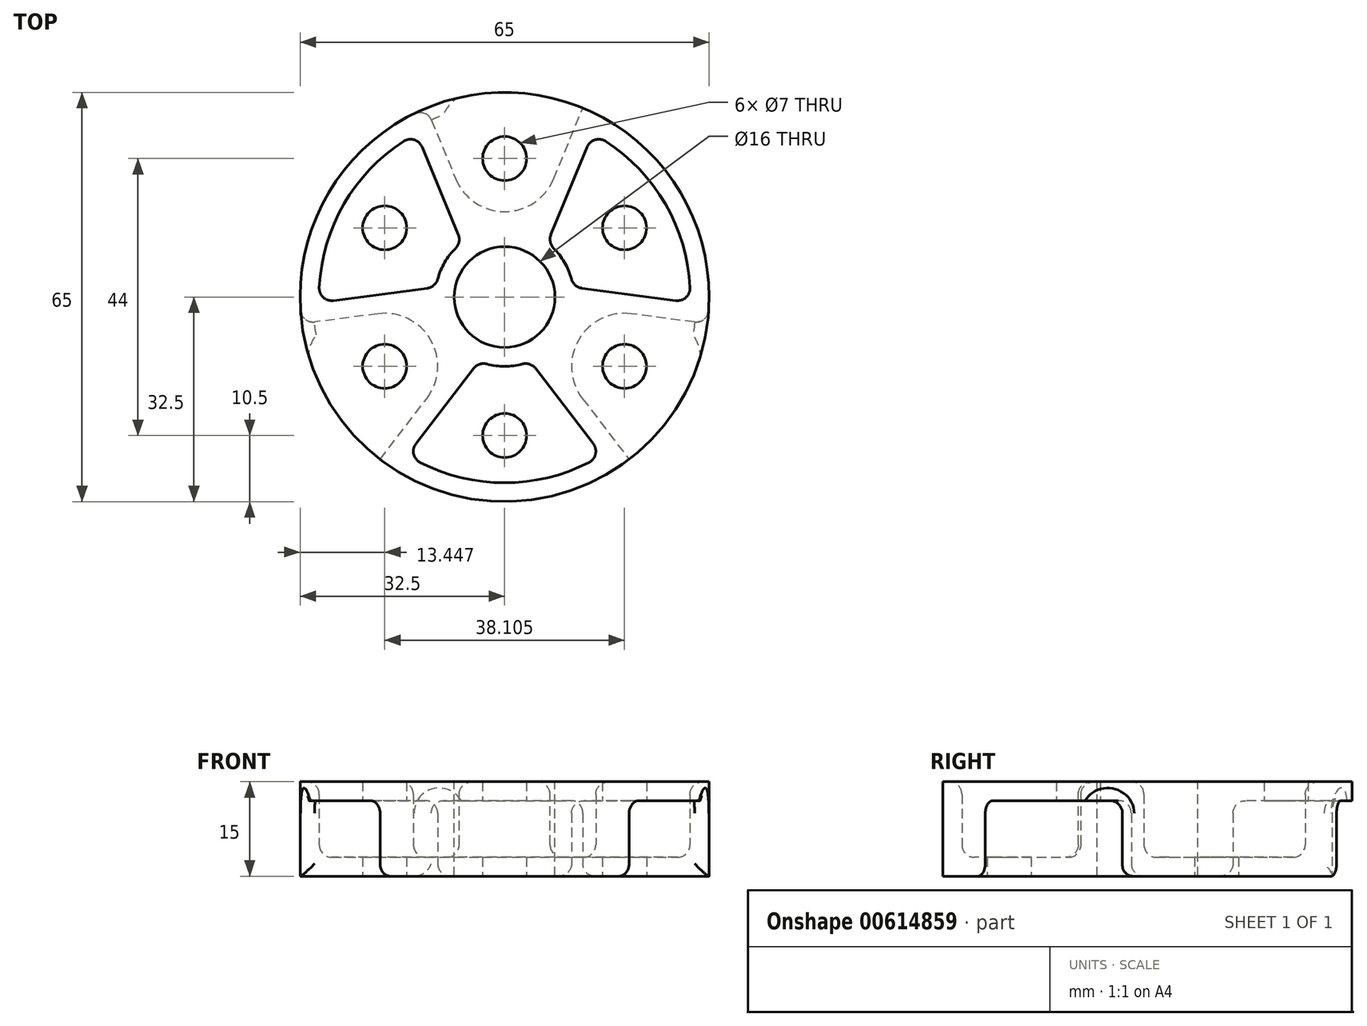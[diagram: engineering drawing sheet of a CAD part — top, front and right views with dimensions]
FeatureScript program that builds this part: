
annotation { "Feature Type Name" : "Feature", "Feature Type Description" : "" }
export const myFeature = defineFeature(function(context is Context, id is Id, definition is map)
    precondition{}
    {
        {
            var Q0;
            Q0=qCreatedBy(makeId("Top.planeOp"),FACE);
            var sketch = newSketch(context, id + "F0", { "sketchPlane" : qUnion([Q0])});
            skCircle(sketch, "E0", {"center": v(0, 0) * mm, "radius": 32.5 * mm});
            skCircle(sketch, "E1", {"center": v(0, 0) * mm, "radius": 8 * mm});
            skCircle(sketch, "E2", {"center": v(19.05, 11) * mm, "radius": 3.5 * mm});
            skCircle(sketch, "E3", {"center": v(0, 0) * mm, "radius": 22 * mm, "construction": true});
            skCircle(sketch, "E4.1.0", {"center": v(0, 22) * mm, "radius": 3.5 * mm});
            skCircle(sketch, "E4.2.0", {"center": v(-19.05, 11) * mm, "radius": 3.5 * mm});
            skCircle(sketch, "E4.3.0", {"center": v(-19.05, -11) * mm, "radius": 3.5 * mm});
            skLineSegment(sketch, "E5", {"start": v(-12.44, 30.03) * mm, "end": v(-7.78, 18.78) * mm});
            skArc(sketch, "E6", {"start": v(-7.78, 18.78) * mm, "mid": v(0, 13.58) * mm, "end": v(7.78, 18.78) * mm});
            skLineSegment(sketch, "E7", {"start": v(7.78, 18.78) * mm, "end": v(12.44, 30.03) * mm});
            skLineSegment(sketch, "E8.1.0", {"start": v(-20.15, -2.65) * mm, "end": v(-32.22, -4.24) * mm});
            skArc(sketch, "E8.1.1", {"start": v(-12.37, -16.13) * mm, "mid": v(-11.76, -6.8) * mm, "end": v(-20.15, -2.65) * mm});
            skLineSegment(sketch, "E8.1.2", {"start": v(-19.78, -25.78) * mm, "end": v(-12.37, -16.13) * mm});
            skCircle(sketch, "E9.0", {"center": v(0, 0) * mm, "radius": 29.5 * mm});
            skLineSegment(sketch, "E10.0", {"start": v(10.55, 17.63) * mm, "end": v(15.16, 28.75) * mm});
            skArc(sketch, "E10.1", {"start": v(-10.55, 17.63) * mm, "mid": v(0, 10.58) * mm, "end": v(10.55, 17.63) * mm});
            skLineSegment(sketch, "E10.2", {"start": v(-15.16, 28.75) * mm, "end": v(-10.55, 17.63) * mm});
            skLineSegment(sketch, "E11.0", {"start": v(10, -17.95) * mm, "end": v(17.32, -27.5) * mm});
            skArc(sketch, "E11.1", {"start": v(20.54, 0.32) * mm, "mid": v(9.16, -5.3) * mm, "end": v(10, -17.95) * mm});
            skLineSegment(sketch, "E11.2", {"start": v(32.48, -1.25) * mm, "end": v(20.54, 0.32) * mm});
            skCircle(sketch, "E12.1.4.0", {"center": v(0, -22) * mm, "radius": 3.5 * mm});
            skCircle(sketch, "E12.1.5.0", {"center": v(19.05, -11) * mm, "radius": 3.5 * mm});
            skLineSegment(sketch, "E13.1.2.0", {"start": v(12.37, -16.13) * mm, "end": v(19.78, -25.78) * mm});
            skArc(sketch, "E13.3.2.0", {"start": v(20.15, -2.65) * mm, "mid": v(11.76, -6.8) * mm, "end": v(12.37, -16.13) * mm});
            skLineSegment(sketch, "E13.7.2.0", {"start": v(32.22, -4.24) * mm, "end": v(20.15, -2.65) * mm});
            skLineSegment(sketch, "E14.0", {"start": v(-20.54, 0.32) * mm, "end": v(-32.61, -1.27) * mm});
            skArc(sketch, "E14.1", {"start": v(-10, -17.95) * mm, "mid": v(-9.16, -5.3) * mm, "end": v(-20.54, 0.32) * mm});
            skLineSegment(sketch, "E14.2", {"start": v(-17.4, -27.61) * mm, "end": v(-10, -17.95) * mm});
            skCircle(sketch, "E15.0", {"center": v(0, 0) * mm, "radius": 11 * mm});
            skLineSegment(sketch, "E16", {"start": v(6.82, 8.63) * mm, "end": v(14, 25.97) * mm});
            skLineSegment(sketch, "E17", {"start": v(10.88, 1.6) * mm, "end": v(29.49, -0.86) * mm});
            skLineSegment(sketch, "E18.1.0", {"start": v(-10.88, 1.6) * mm, "end": v(-29.49, -0.86) * mm});
            skLineSegment(sketch, "E18.1.1", {"start": v(-6.82, 8.63) * mm, "end": v(-14, 25.97) * mm});
            skLineSegment(sketch, "E18.2.0", {"start": v(4.06, -10.22) * mm, "end": v(15.49, -25.1) * mm});
            skLineSegment(sketch, "E18.2.1", {"start": v(-4.06, -10.22) * mm, "end": v(-15.49, -25.1) * mm});
            skSolve(sketch);
        }
        {
            var Q0;
            {var subQ7=sQuery(id+"F0.wireOp",EDGE,"E8.1.1");Q0=makeQuery(id+"F0.imprint","IMPRINT",FACE,{"disambiguationData":[TD([[makeQuery(id+"F0.imprint","IMPRINT",EDGE,{"derivedFrom":subQ7}),-1.0]])]});}
            var Q1;
            {var subQ0=sQuery(id+"F0.wireOp",EDGE,"E8.1.2");var subQ1=sQuery(id+"F0.wireOp",EDGE,"E0");var subQ2=makeQuery(id+"F0.imprint","INTERSECT",VERTEX,{"derivedFrom":[subQ1,subQ0]});Q1=makeQuery(id+"F0.imprint","IMPRINT",FACE,{"disambiguationData":[TD([[makeQuery(id+"F0.imprint","IMPRINT",EDGE,{"disambiguationData":[TD([[subQ2,-1.0]])],"derivedFrom":subQ1}),1.0]])]});}
            var Q2;
            Q2=makeQuery(id+"F0.imprint","IMPRINT",FACE,{"disambiguationData":[TD([[makeQuery(id+"F0.imprint","IMPRINT",EDGE,{"derivedFrom":sQuery(id+"F0.wireOp",EDGE,"E4.3.0")}),-1.0]])]});
            var Q3;
            {var subQ0=sQuery(id+"F0.wireOp",EDGE,"E8.1.0");var subQ1=sQuery(id+"F0.wireOp",EDGE,"E0");var subQ2=makeQuery(id+"F0.imprint","INTERSECT",VERTEX,{"derivedFrom":[subQ1,subQ0]});Q3=makeQuery(id+"F0.imprint","IMPRINT",FACE,{"disambiguationData":[TD([[makeQuery(id+"F0.imprint","IMPRINT",EDGE,{"disambiguationData":[TD([[subQ2,-1.0]])],"derivedFrom":subQ1}),1.0]])]});}
            var Q4;
            {var subQ0=sQuery(id+"F0.wireOp",EDGE,"E8.1.0");var subQ1=sQuery(id+"F0.wireOp",EDGE,"E0");var subQ2=makeQuery(id+"F0.imprint","INTERSECT",VERTEX,{"derivedFrom":[subQ1,subQ0]});Q4=makeQuery(id+"F0.imprint","IMPRINT",FACE,{"disambiguationData":[TD([[makeQuery(id+"F0.imprint","IMPRINT",EDGE,{"disambiguationData":[TD([[subQ2,1.0]])],"derivedFrom":subQ1}),1.0]])]});}
            var Q5;
            {var subQ0=sQuery(id+"F0.wireOp",EDGE,"E7");var subQ1=sQuery(id+"F0.wireOp",EDGE,"E0");var subQ2=makeQuery(id+"F0.imprint","INTERSECT",VERTEX,{"derivedFrom":[subQ1,subQ0]});Q5=makeQuery(id+"F0.imprint","IMPRINT",FACE,{"disambiguationData":[TD([[makeQuery(id+"F0.imprint","IMPRINT",EDGE,{"disambiguationData":[TD([[subQ2,1.0]])],"derivedFrom":subQ1}),1.0]])]});}
            var Q6;
            {var subQ0=sQuery(id+"F0.wireOp",EDGE,"E5");var subQ1=sQuery(id+"F0.wireOp",EDGE,"E0");var subQ2=makeQuery(id+"F0.imprint","INTERSECT",VERTEX,{"derivedFrom":[subQ1,subQ0]});Q6=makeQuery(id+"F0.imprint","IMPRINT",FACE,{"disambiguationData":[TD([[makeQuery(id+"F0.imprint","IMPRINT",EDGE,{"disambiguationData":[TD([[subQ2,1.0]])],"derivedFrom":subQ1}),1.0]])]});}
            var Q7;
            Q7=makeQuery(id+"F0.imprint","IMPRINT",FACE,{"disambiguationData":[TD([[makeQuery(id+"F0.imprint","IMPRINT",EDGE,{"derivedFrom":sQuery(id+"F0.wireOp",EDGE,"E4.1.0")}),-1.0]])]});
            var Q8;
            {var subQ5=sQuery(id+"F0.wireOp",EDGE,"E6");Q8=makeQuery(id+"F0.imprint","IMPRINT",FACE,{"disambiguationData":[TD([[makeQuery(id+"F0.imprint","IMPRINT",EDGE,{"derivedFrom":subQ5}),-1.0]])]});}
            var Q9;
            {var subQ0=sQuery(id+"F0.wireOp",EDGE,"E5");var subQ1=sQuery(id+"F0.wireOp",EDGE,"E0");var subQ2=makeQuery(id+"F0.imprint","INTERSECT",VERTEX,{"derivedFrom":[subQ1,subQ0]});Q9=makeQuery(id+"F0.imprint","IMPRINT",FACE,{"disambiguationData":[TD([[makeQuery(id+"F0.imprint","IMPRINT",EDGE,{"disambiguationData":[TD([[subQ2,-1.0]])],"derivedFrom":subQ1}),1.0]])]});}
            var Q10;
            {var subQ0=sQuery(id+"F0.wireOp",EDGE,"E10.0");var subQ1=sQuery(id+"F0.wireOp",EDGE,"E0");var subQ2=makeQuery(id+"F0.imprint","INTERSECT",VERTEX,{"derivedFrom":[subQ1,subQ0]});Q10=makeQuery(id+"F0.imprint","IMPRINT",FACE,{"disambiguationData":[TD([[makeQuery(id+"F0.imprint","IMPRINT",EDGE,{"disambiguationData":[TD([[subQ2,1.0]])],"derivedFrom":subQ1}),1.0]])]});}
            var Q11;
            {var subQ0=sQuery(id+"F0.wireOp",EDGE,"E10.2");var subQ1=sQuery(id+"F0.wireOp",EDGE,"E0");var subQ2=makeQuery(id+"F0.imprint","INTERSECT",VERTEX,{"derivedFrom":[subQ1,subQ0]});Q11=makeQuery(id+"F0.imprint","IMPRINT",FACE,{"disambiguationData":[TD([[makeQuery(id+"F0.imprint","IMPRINT",EDGE,{"disambiguationData":[TD([[subQ2,-1.0]])],"derivedFrom":subQ1}),1.0]])]});}
            var Q12;
            {var subQ0=sQuery(id+"F0.wireOp",EDGE,"E11.1");Q12=makeQuery(id+"F0.imprint","IMPRINT",FACE,{"disambiguationData":[TD([[makeQuery(id+"F0.imprint","IMPRINT",EDGE,{"derivedFrom":subQ0}),1.0]])]});}
            var Q13;
            {var subQ0=sQuery(id+"F0.wireOp",EDGE,"E13.1.2.0");var subQ1=sQuery(id+"F0.wireOp",EDGE,"E0");var subQ2=makeQuery(id+"F0.imprint","INTERSECT",VERTEX,{"derivedFrom":[subQ1,subQ0]});Q13=makeQuery(id+"F0.imprint","IMPRINT",FACE,{"disambiguationData":[TD([[makeQuery(id+"F0.imprint","IMPRINT",EDGE,{"disambiguationData":[TD([[subQ2,-1.0]])],"derivedFrom":subQ1}),1.0]])]});}
            var Q14;
            Q14=makeQuery(id+"F0.imprint","IMPRINT",FACE,{"disambiguationData":[TD([[makeQuery(id+"F0.imprint","IMPRINT",EDGE,{"derivedFrom":sQuery(id+"F0.wireOp",EDGE,"E12.1.5.0")}),-1.0]])]});
            var Q15;
            {var subQ0=sQuery(id+"F0.wireOp",EDGE,"E11.2");var subQ1=sQuery(id+"F0.wireOp",EDGE,"E0");var subQ2=makeQuery(id+"F0.imprint","INTERSECT",VERTEX,{"derivedFrom":[subQ1,subQ0]});Q15=makeQuery(id+"F0.imprint","IMPRINT",FACE,{"disambiguationData":[TD([[makeQuery(id+"F0.imprint","IMPRINT",EDGE,{"disambiguationData":[TD([[subQ2,1.0]])],"derivedFrom":subQ1}),1.0]])]});}
            var Q16;
            {var subQ0=sQuery(id+"F0.wireOp",EDGE,"E11.0");var subQ1=sQuery(id+"F0.wireOp",EDGE,"E0");var subQ2=makeQuery(id+"F0.imprint","INTERSECT",VERTEX,{"derivedFrom":[subQ1,subQ0]});Q16=makeQuery(id+"F0.imprint","IMPRINT",FACE,{"disambiguationData":[TD([[makeQuery(id+"F0.imprint","IMPRINT",EDGE,{"disambiguationData":[TD([[subQ2,1.0]])],"derivedFrom":subQ1}),1.0]])]});}
            var Q17;
            {var subQ0=sQuery(id+"F0.wireOp",EDGE,"E11.0");var subQ1=sQuery(id+"F0.wireOp",EDGE,"E0");var subQ2=makeQuery(id+"F0.imprint","INTERSECT",VERTEX,{"derivedFrom":[subQ1,subQ0]});Q17=makeQuery(id+"F0.imprint","IMPRINT",FACE,{"disambiguationData":[TD([[makeQuery(id+"F0.imprint","IMPRINT",EDGE,{"disambiguationData":[TD([[subQ2,-1.0]])],"derivedFrom":subQ1}),1.0]])]});}
            var Q18;
            {var subQ0=sQuery(id+"F0.wireOp",EDGE,"E15.0");var subQ1=sQuery(id+"F0.wireOp",EDGE,"E11.1");var subQ2=makeQuery(id+"F0.imprint","INTERSECT",VERTEX,{"disambiguationData":[OD(0.0)],"derivedFrom":[subQ1,subQ0]});Q18=makeQuery(id+"F0.imprint","IMPRINT",FACE,{"disambiguationData":[TD([[makeQuery(id+"F0.imprint","IMPRINT",EDGE,{"disambiguationData":[TD([[subQ2,-1.0]])],"derivedFrom":subQ1}),1.0]])]});}
            var Q19;
            {var subQ0=sQuery(id+"F0.wireOp",EDGE,"E15.0");var subQ1=sQuery(id+"F0.wireOp",EDGE,"E14.1");var subQ2=makeQuery(id+"F0.imprint","INTERSECT",VERTEX,{"disambiguationData":[OD(0.0)],"derivedFrom":[subQ1,subQ0]});Q19=makeQuery(id+"F0.imprint","IMPRINT",FACE,{"disambiguationData":[TD([[makeQuery(id+"F0.imprint","IMPRINT",EDGE,{"disambiguationData":[TD([[subQ2,-1.0]])],"derivedFrom":subQ1}),1.0]])]});}
            var Q20;
            {var subQ0=sQuery(id+"F0.wireOp",EDGE,"E15.0");var subQ1=sQuery(id+"F0.wireOp",EDGE,"E10.1");var subQ2=makeQuery(id+"F0.imprint","INTERSECT",VERTEX,{"disambiguationData":[OD(0.0)],"derivedFrom":[subQ1,subQ0]});Q20=makeQuery(id+"F0.imprint","IMPRINT",FACE,{"disambiguationData":[TD([[makeQuery(id+"F0.imprint","IMPRINT",EDGE,{"disambiguationData":[TD([[subQ2,-1.0]])],"derivedFrom":subQ1}),1.0]])]});}
            extrude(context, id + "F1", {"entities" : qUnion([Q0, Q1, Q2, Q3, Q4, Q5, Q6, Q7, Q8, Q9, Q10, Q11, Q12, Q13, Q14, Q15, Q16, Q17, Q18, Q19, Q20]), "endBound" : BoundingType.SYMMETRIC, "depth" : 15 * mm, "offsetDistance" : 25 * mm});
        }
        {
            var Q0;
            Q0=makeQuery(id+"F1.opExtrude","CAP_FACE",FACE,{"disambiguationData":[OSD([sQuery(id+"F0.wireOp",EDGE,"E0"),sQuery(id+"F0.wireOp",EDGE,"E4.1.0"),sQuery(id+"F0.wireOp",EDGE,"E4.3.0"),sQuery(id+"F0.wireOp",EDGE,"E9.0"),sQuery(id+"F0.wireOp",EDGE,"E10.0"),sQuery(id+"F0.wireOp",EDGE,"E10.1"),sQuery(id+"F0.wireOp",EDGE,"E10.2"),sQuery(id+"F0.wireOp",EDGE,"E11.0"),sQuery(id+"F0.wireOp",EDGE,"E11.1"),sQuery(id+"F0.wireOp",EDGE,"E11.2")])],"isStart":true});
            var sketch = newSketch(context, id + "F2", { "sketchPlane" : qUnion([Q0])});
            skLineSegment(sketch, "E19.0", {"start": v(-20.15, 2.65) * mm, "end": v(-32.22, 4.24) * mm});
            skArc(sketch, "E20.0", {"start": v(-12.37, 16.13) * mm, "mid": v(-11.76, 6.8) * mm, "end": v(-20.15, 2.65) * mm});
            skLineSegment(sketch, "E21.0", {"start": v(-19.78, 25.78) * mm, "end": v(-12.37, 16.13) * mm});
            skCircle(sketch, "E22.0", {"center": v(0, 0) * mm, "radius": 32.5 * mm});
            skLineSegment(sketch, "E23.0", {"start": v(-12.44, -30.03) * mm, "end": v(-7.78, -18.78) * mm});
            skArc(sketch, "E24.0", {"start": v(-7.78, -18.78) * mm, "mid": v(0, -13.58) * mm, "end": v(7.78, -18.78) * mm});
            skLineSegment(sketch, "E25.0", {"start": v(7.78, -18.78) * mm, "end": v(12.44, -30.03) * mm});
            skLineSegment(sketch, "E26.0", {"start": v(32.22, 4.24) * mm, "end": v(20.15, 2.65) * mm});
            skArc(sketch, "E27.0", {"start": v(20.15, 2.65) * mm, "mid": v(11.76, 6.8) * mm, "end": v(12.37, 16.13) * mm});
            skLineSegment(sketch, "E28.0", {"start": v(12.37, 16.13) * mm, "end": v(19.78, 25.78) * mm});
            skSolve(sketch);
        }
        {
            var Q0;
            {var subQ2=sQuery(id+"F2.wireOp",EDGE,"E19.0");Q0=makeQuery(id+"F2.imprint","IMPRINT",FACE,{"disambiguationData":[TD([[makeQuery(id+"F2.imprint","IMPRINT",EDGE,{"derivedFrom":subQ2}),-1.0]])]});}
            var Q1;
            {var subQ1=sQuery(id+"F2.wireOp",EDGE,"E23.0");Q1=makeQuery(id+"F2.imprint","IMPRINT",FACE,{"disambiguationData":[TD([[makeQuery(id+"F2.imprint","IMPRINT",EDGE,{"derivedFrom":subQ1}),-1.0]])]});}
            var Q2;
            {var subQ1=sQuery(id+"F2.wireOp",EDGE,"E26.0");Q2=makeQuery(id+"F2.imprint","IMPRINT",FACE,{"disambiguationData":[TD([[makeQuery(id+"F2.imprint","IMPRINT",EDGE,{"derivedFrom":subQ1}),-1.0]])]});}
            var Q3;
            Q3=makeQuery(id+"F1.opExtrude","CAP_FACE",FACE,{"disambiguationData":[OSD([sQuery(id+"F0.wireOp",EDGE,"E0"),sQuery(id+"F0.wireOp",EDGE,"E4.1.0"),sQuery(id+"F0.wireOp",EDGE,"E4.3.0"),sQuery(id+"F0.wireOp",EDGE,"E9.0"),sQuery(id+"F0.wireOp",EDGE,"E10.0"),sQuery(id+"F0.wireOp",EDGE,"E10.1"),sQuery(id+"F0.wireOp",EDGE,"E10.2"),sQuery(id+"F0.wireOp",EDGE,"E11.0"),sQuery(id+"F0.wireOp",EDGE,"E11.1"),sQuery(id+"F0.wireOp",EDGE,"E11.2")])],"isStart":false});
            extrude(context, id + "F3", {"entities" : qUnion([Q0, Q1, Q2]), "operationType" : NewBodyOperationType.REMOVE, "endBound" : BoundingType.UP_TO_SURFACE, "oppositeDirection" : true, "depth" : 25 * mm, "endBoundEntityFace" : qUnion([Q3]), "hasOffset" : true, "offsetDistance" : 3 * mm});
        }
        {
            var Q0;
            Q0=makeQuery(id+"F0.imprint","IMPRINT",FACE,{"disambiguationData":[TD([[makeQuery(id+"F0.imprint","IMPRINT",EDGE,{"derivedFrom":sQuery(id+"F0.wireOp",EDGE,"E1")}),-1.0]])]});
            var Q1;
            {var subQ0=sQuery(id+"F0.wireOp",EDGE,"E16");var subQ1=sQuery(id+"F0.wireOp",EDGE,"E10.1");var subQ2=makeQuery(id+"F0.imprint","INTERSECT",VERTEX,{"derivedFrom":[subQ1,subQ0]});Q1=makeQuery(id+"F0.imprint","IMPRINT",FACE,{"disambiguationData":[TD([[makeQuery(id+"F0.imprint","IMPRINT",EDGE,{"disambiguationData":[TD([[subQ2,1.0]])],"derivedFrom":subQ1}),-1.0]])]});}
            var Q2;
            {var subQ0=sQuery(id+"F0.wireOp",EDGE,"E17");var subQ1=sQuery(id+"F0.wireOp",EDGE,"E11.1");var subQ2=makeQuery(id+"F0.imprint","INTERSECT",VERTEX,{"derivedFrom":[subQ1,subQ0]});Q2=makeQuery(id+"F0.imprint","IMPRINT",FACE,{"disambiguationData":[TD([[makeQuery(id+"F0.imprint","IMPRINT",EDGE,{"disambiguationData":[TD([[subQ2,-1.0]])],"derivedFrom":subQ1}),-1.0]])]});}
            var Q3;
            {var subQ0=sQuery(id+"F0.wireOp",EDGE,"E18.2.0");var subQ1=sQuery(id+"F0.wireOp",EDGE,"E11.1");var subQ2=makeQuery(id+"F0.imprint","INTERSECT",VERTEX,{"derivedFrom":[subQ1,subQ0]});Q3=makeQuery(id+"F0.imprint","IMPRINT",FACE,{"disambiguationData":[TD([[makeQuery(id+"F0.imprint","IMPRINT",EDGE,{"disambiguationData":[TD([[subQ2,1.0]])],"derivedFrom":subQ1}),-1.0]])]});}
            var Q4;
            {var subQ0=sQuery(id+"F0.wireOp",EDGE,"E18.2.1");var subQ1=sQuery(id+"F0.wireOp",EDGE,"E14.1");var subQ2=makeQuery(id+"F0.imprint","INTERSECT",VERTEX,{"derivedFrom":[subQ1,subQ0]});Q4=makeQuery(id+"F0.imprint","IMPRINT",FACE,{"disambiguationData":[TD([[makeQuery(id+"F0.imprint","IMPRINT",EDGE,{"disambiguationData":[TD([[subQ2,-1.0]])],"derivedFrom":subQ1}),-1.0]])]});}
            var Q5;
            {var subQ0=sQuery(id+"F0.wireOp",EDGE,"E18.1.0");var subQ1=sQuery(id+"F0.wireOp",EDGE,"E14.1");var subQ2=makeQuery(id+"F0.imprint","INTERSECT",VERTEX,{"derivedFrom":[subQ1,subQ0]});Q5=makeQuery(id+"F0.imprint","IMPRINT",FACE,{"disambiguationData":[TD([[makeQuery(id+"F0.imprint","IMPRINT",EDGE,{"disambiguationData":[TD([[subQ2,1.0]])],"derivedFrom":subQ1}),-1.0]])]});}
            var Q6;
            {var subQ0=sQuery(id+"F0.wireOp",EDGE,"E18.1.1");var subQ1=sQuery(id+"F0.wireOp",EDGE,"E10.1");var subQ2=makeQuery(id+"F0.imprint","INTERSECT",VERTEX,{"derivedFrom":[subQ1,subQ0]});Q6=makeQuery(id+"F0.imprint","IMPRINT",FACE,{"disambiguationData":[TD([[makeQuery(id+"F0.imprint","IMPRINT",EDGE,{"disambiguationData":[TD([[subQ2,-1.0]])],"derivedFrom":subQ1}),-1.0]])]});}
            var Q7;
            Q7=makeQuery(id+"F1.opExtrude","CAP_FACE",FACE,{"disambiguationData":[OSD([sQuery(id+"F0.wireOp",EDGE,"E0"),sQuery(id+"F0.wireOp",EDGE,"E4.1.0"),sQuery(id+"F0.wireOp",EDGE,"E4.3.0"),sQuery(id+"F0.wireOp",EDGE,"E9.0"),sQuery(id+"F0.wireOp",EDGE,"E10.0"),sQuery(id+"F0.wireOp",EDGE,"E10.1"),sQuery(id+"F0.wireOp",EDGE,"E10.2"),sQuery(id+"F0.wireOp",EDGE,"E11.0"),sQuery(id+"F0.wireOp",EDGE,"E11.1"),sQuery(id+"F0.wireOp",EDGE,"E11.2")])],"isStart":true});
            var Q8;
            Q8=makeQuery(id+"F1.opExtrude","CAP_FACE",FACE,{"disambiguationData":[OSD([sQuery(id+"F0.wireOp",EDGE,"E0"),sQuery(id+"F0.wireOp",EDGE,"E4.1.0"),sQuery(id+"F0.wireOp",EDGE,"E4.3.0"),sQuery(id+"F0.wireOp",EDGE,"E9.0"),sQuery(id+"F0.wireOp",EDGE,"E10.0"),sQuery(id+"F0.wireOp",EDGE,"E10.1"),sQuery(id+"F0.wireOp",EDGE,"E10.2"),sQuery(id+"F0.wireOp",EDGE,"E11.0"),sQuery(id+"F0.wireOp",EDGE,"E11.1"),sQuery(id+"F0.wireOp",EDGE,"E11.2"),sQuery(id+"F0.wireOp",EDGE,"E12.1.5.0"),sQuery(id+"F0.wireOp",EDGE,"E14.0"),sQuery(id+"F0.wireOp",EDGE,"E14.1"),sQuery(id+"F0.wireOp",EDGE,"E14.2")])],"isStart":false});
            extrude(context, id + "F4", {"entities" : qUnion([Q0, Q1, Q2, Q3, Q4, Q5, Q6]), "operationType" : NewBodyOperationType.ADD, "endBound" : BoundingType.UP_TO_SURFACE, "oppositeDirection" : true, "depth" : 25 * mm, "endBoundEntityFace" : qUnion([Q7]), "offsetDistance" : 25 * mm, "hasSecondDirection" : true, "secondDirectionBound" : SecondDirectionBoundingType.UP_TO_SURFACE, "secondDirectionOppositeDirection" : false, "secondDirectionDepth" : 25 * mm, "secondDirectionBoundEntityFace" : qUnion([Q8])});
        }
        {
            var Q0;
            {var subQ0=sQuery(id+"F0.wireOp",EDGE,"E18.2.1");var subQ1=sQuery(id+"F0.wireOp",EDGE,"E18.2.0");var subQ2=sQuery(id+"F0.wireOp",EDGE,"E18.1.1");var subQ3=sQuery(id+"F0.wireOp",EDGE,"E18.1.0");var subQ4=sQuery(id+"F0.wireOp",EDGE,"E17");var subQ5=sQuery(id+"F0.wireOp",EDGE,"E16");var subQ6=sQuery(id+"F0.wireOp",EDGE,"E14.1");var subQ7=sQuery(id+"F0.wireOp",EDGE,"E12.1.5.0");var subQ8=sQuery(id+"F0.wireOp",EDGE,"E11.1");var subQ9=sQuery(id+"F0.wireOp",EDGE,"E10.1");var subQ10=sQuery(id+"F0.wireOp",EDGE,"E9.0");var subQ11=sQuery(id+"F0.wireOp",EDGE,"E4.3.0");var subQ12=sQuery(id+"F0.wireOp",EDGE,"E4.1.0");var subQ13=sQuery(id+"F0.wireOp",EDGE,"E0");Q0=makeQuery(id+"F4.boolean.opBoolean","MERGE",FACE,{"derivedFrom":[makeQuery(id+"F1.opExtrude","CAP_FACE",FACE,{"disambiguationData":[OSD([subQ13,subQ12,subQ11,subQ10,subQ9,subQ8,subQ7,subQ6,subQ5,subQ4,subQ3,subQ2,subQ1,subQ0])],"isStart":true}),makeQuery(id+"F4.opExtrude","CAP_FACE",FACE,{"disambiguationData":[OSD([subQ13,subQ12,subQ11,subQ10,subQ9,subQ8,subQ7,subQ6,subQ5,subQ4,subQ3,subQ2,subQ1,subQ0])],"isStart":false})]});}
            var sketch = newSketch(context, id + "F5", { "sketchPlane" : qUnion([Q0])});
            skArc(sketch, "E29.0.0", {"start": v(-7.78, -18.78) * mm, "mid": v(0, -13.58) * mm, "end": v(7.78, -18.78) * mm});
            skLineSegment(sketch, "E29.0.1", {"start": v(7.78, -18.78) * mm, "end": v(12.44, -30.03) * mm});
            skArc(sketch, "E29.0.2", {"start": v(12.44, -30.03) * mm, "mid": v(28.15, -16.25) * mm, "end": v(32.22, 4.24) * mm});
            skLineSegment(sketch, "E29.0.3", {"start": v(32.22, 4.24) * mm, "end": v(20.15, 2.65) * mm});
            skArc(sketch, "E29.0.4", {"start": v(20.15, 2.65) * mm, "mid": v(11.76, 6.8) * mm, "end": v(12.37, 16.13) * mm});
            skLineSegment(sketch, "E29.0.5", {"start": v(12.37, 16.13) * mm, "end": v(19.78, 25.78) * mm});
            skArc(sketch, "E29.0.6", {"start": v(19.78, 25.78) * mm, "mid": v(0, 32.5) * mm, "end": v(-19.78, 25.78) * mm});
            skLineSegment(sketch, "E29.0.7", {"start": v(-19.78, 25.78) * mm, "end": v(-12.37, 16.13) * mm});
            skArc(sketch, "E29.0.8", {"start": v(-12.37, 16.13) * mm, "mid": v(-11.76, 6.8) * mm, "end": v(-20.15, 2.65) * mm});
            skLineSegment(sketch, "E29.0.9", {"start": v(-20.15, 2.65) * mm, "end": v(-32.22, 4.24) * mm});
            skArc(sketch, "E29.0.10", {"start": v(-32.22, 4.24) * mm, "mid": v(-28.15, -16.25) * mm, "end": v(-12.44, -30.03) * mm});
            skLineSegment(sketch, "E29.0.11", {"start": v(-12.44, -30.03) * mm, "end": v(-7.78, -18.78) * mm});
            skCircle(sketch, "E30.0", {"center": v(-19.05, -11) * mm, "radius": 3.5 * mm});
            skCircle(sketch, "E31.0", {"center": v(0, 22) * mm, "radius": 3.5 * mm});
            skCircle(sketch, "E32.0", {"center": v(19.05, -11) * mm, "radius": 3.5 * mm});
            skSolve(sketch);
        }
        {
            var Q0;
            {var subQ0=sQuery(id+"F0.wireOp",EDGE,"E18.2.0");var subQ1=sQuery(id+"F0.wireOp",EDGE,"E9.0");Q0=makeQuery(id+"F5.imprint","IMPRINT",FACE,{"disambiguationData":[TD([[makeQuery(id+"F5.imprint","IMPRINT",EDGE,{"derivedFrom":makeQuery(id+"F1.opExtrude","CAP_EDGE",EDGE,{"disambiguationData":[OSD([subQ1]),TDD([makeQuery(id+"F0.imprint","IMPRINT",EDGE,{"disambiguationData":[TD([[makeQuery(id+"F0.imprint","INTERSECT",VERTEX,{"derivedFrom":[subQ1,sQuery(id+"F0.wireOp",EDGE,"E11.0"),subQ0]}),1.0]])],"derivedFrom":subQ1})])],"isStart":true})}),-1.0]])]});}
            var Q1;
            {var subQ0=sQuery(id+"F0.wireOp",EDGE,"E18.1.1");var subQ1=sQuery(id+"F0.wireOp",EDGE,"E9.0");Q1=makeQuery(id+"F5.imprint","IMPRINT",FACE,{"disambiguationData":[TD([[makeQuery(id+"F5.imprint","IMPRINT",EDGE,{"derivedFrom":makeQuery(id+"F1.opExtrude","CAP_EDGE",EDGE,{"disambiguationData":[OSD([subQ1]),TDD([makeQuery(id+"F0.imprint","IMPRINT",EDGE,{"disambiguationData":[TD([[makeQuery(id+"F0.imprint","INTERSECT",VERTEX,{"derivedFrom":[subQ1,sQuery(id+"F0.wireOp",EDGE,"E10.2"),subQ0]}),-1.0]])],"derivedFrom":subQ1})])],"isStart":true})}),-1.0]])]});}
            var Q2;
            {var subQ0=sQuery(id+"F0.wireOp",EDGE,"E16");var subQ1=sQuery(id+"F0.wireOp",EDGE,"E9.0");Q2=makeQuery(id+"F5.imprint","IMPRINT",FACE,{"disambiguationData":[TD([[makeQuery(id+"F5.imprint","IMPRINT",EDGE,{"derivedFrom":makeQuery(id+"F1.opExtrude","CAP_EDGE",EDGE,{"disambiguationData":[OSD([subQ1]),TDD([makeQuery(id+"F0.imprint","IMPRINT",EDGE,{"disambiguationData":[TD([[makeQuery(id+"F0.imprint","INTERSECT",VERTEX,{"derivedFrom":[subQ1,sQuery(id+"F0.wireOp",EDGE,"E10.0"),subQ0]}),1.0]])],"derivedFrom":subQ1})])],"isStart":true})}),-1.0]])]});}
            extrude(context, id + "F6", {"entities" : qUnion([Q0, Q1, Q2]), "operationType" : NewBodyOperationType.ADD, "oppositeDirection" : true, "depth" : 3 * mm, "offsetDistance" : 25 * mm});
        }
        {
            var Q0;
            Q0=makeQuery(id+"F3.boolean.opBoolean","COPY",FACE,{"derivedFrom":makeQuery(id+"F3.opExtrude","SWEPT_FACE",FACE,{"disambiguationData":[OSD([sQuery(id+"F2.wireOp",EDGE,"E19.0")])]})});
            var Q1;
            Q1=makeQuery(id+"F3.boolean.opBoolean","COPY",FACE,{"derivedFrom":makeQuery(id+"F3.opExtrude","SWEPT_FACE",FACE,{"disambiguationData":[OSD([sQuery(id+"F2.wireOp",EDGE,"E26.0")])]})});
            var Q2;
            Q2=makeQuery(id+"F3.boolean.opBoolean","COPY",FACE,{"derivedFrom":makeQuery(id+"F3.opExtrude","SWEPT_FACE",FACE,{"disambiguationData":[OSD([sQuery(id+"F2.wireOp",EDGE,"E23.0")])]})});
            var Q3;
            {var subQ0=sQuery(id+"F0.wireOp",EDGE,"E15.0");Q3=makeQuery(id+"F4.opExtrude","SWEPT_FACE",FACE,{"disambiguationData":[OSD([subQ0]),TDD([makeQuery(id+"F0.imprint","IMPRINT",EDGE,{"disambiguationData":[TD([[makeQuery(id+"F0.imprint","INTERSECT",VERTEX,{"derivedFrom":[subQ0,sQuery(id+"F0.wireOp",EDGE,"E18.2.0")]}),1.0]])],"derivedFrom":subQ0})])]});}
            var Q4;
            {var subQ0=sQuery(id+"F0.wireOp",EDGE,"E18.2.1");Q4=makeQuery(id+"F4.boolean.opBoolean","MERGE",FACE,{"derivedFrom":[makeQuery(id+"F1.opExtrude","SWEPT_FACE",FACE,{"disambiguationData":[OSD([subQ0])]}),makeQuery(id+"F4.opExtrude","SWEPT_FACE",FACE,{"disambiguationData":[OSD([subQ0])]})]});}
            var Q5;
            {var subQ0=sQuery(id+"F0.wireOp",EDGE,"E18.2.0");Q5=makeQuery(id+"F4.boolean.opBoolean","MERGE",FACE,{"derivedFrom":[makeQuery(id+"F1.opExtrude","SWEPT_FACE",FACE,{"disambiguationData":[OSD([subQ0])]}),makeQuery(id+"F4.opExtrude","SWEPT_FACE",FACE,{"disambiguationData":[OSD([subQ0])]})]});}
            var Q6;
            {var subQ0=sQuery(id+"F0.wireOp",EDGE,"E9.0");Q6=makeQuery(id+"F1.opExtrude","SWEPT_FACE",FACE,{"disambiguationData":[OSD([subQ0]),TDD([makeQuery(id+"F0.imprint","IMPRINT",EDGE,{"disambiguationData":[TD([[makeQuery(id+"F0.imprint","INTERSECT",VERTEX,{"derivedFrom":[subQ0,sQuery(id+"F0.wireOp",EDGE,"E11.0"),sQuery(id+"F0.wireOp",EDGE,"E18.2.0")]}),1.0]])],"derivedFrom":subQ0})])]});}
            var Q7;
            {var subQ0=sQuery(id+"F0.wireOp",EDGE,"E16");Q7=makeQuery(id+"F4.boolean.opBoolean","MERGE",FACE,{"derivedFrom":[makeQuery(id+"F1.opExtrude","SWEPT_FACE",FACE,{"disambiguationData":[OSD([subQ0])]}),makeQuery(id+"F4.opExtrude","SWEPT_FACE",FACE,{"disambiguationData":[OSD([subQ0])]})]});}
            var Q8;
            {var subQ0=sQuery(id+"F0.wireOp",EDGE,"E9.0");Q8=makeQuery(id+"F1.opExtrude","SWEPT_FACE",FACE,{"disambiguationData":[OSD([subQ0]),TDD([makeQuery(id+"F0.imprint","IMPRINT",EDGE,{"disambiguationData":[TD([[makeQuery(id+"F0.imprint","INTERSECT",VERTEX,{"derivedFrom":[subQ0,sQuery(id+"F0.wireOp",EDGE,"E10.0"),sQuery(id+"F0.wireOp",EDGE,"E16")]}),1.0]])],"derivedFrom":subQ0})])]});}
            var Q9;
            {var subQ0=sQuery(id+"F0.wireOp",EDGE,"E15.0");Q9=makeQuery(id+"F4.opExtrude","SWEPT_FACE",FACE,{"disambiguationData":[OSD([subQ0]),TDD([makeQuery(id+"F0.imprint","IMPRINT",EDGE,{"disambiguationData":[TD([[makeQuery(id+"F0.imprint","INTERSECT",VERTEX,{"derivedFrom":[subQ0,sQuery(id+"F0.wireOp",EDGE,"E16")]}),1.0]])],"derivedFrom":subQ0})])]});}
            var Q10;
            {var subQ0=sQuery(id+"F0.wireOp",EDGE,"E17");Q10=makeQuery(id+"F4.boolean.opBoolean","MERGE",FACE,{"derivedFrom":[makeQuery(id+"F1.opExtrude","SWEPT_FACE",FACE,{"disambiguationData":[OSD([subQ0])]}),makeQuery(id+"F4.opExtrude","SWEPT_FACE",FACE,{"disambiguationData":[OSD([subQ0])]})]});}
            var Q11;
            {var subQ0=sQuery(id+"F0.wireOp",EDGE,"E18.1.0");Q11=makeQuery(id+"F4.boolean.opBoolean","MERGE",FACE,{"derivedFrom":[makeQuery(id+"F1.opExtrude","SWEPT_FACE",FACE,{"disambiguationData":[OSD([subQ0])]}),makeQuery(id+"F4.opExtrude","SWEPT_FACE",FACE,{"disambiguationData":[OSD([subQ0])]})]});}
            var Q12;
            {var subQ0=sQuery(id+"F0.wireOp",EDGE,"E9.0");Q12=makeQuery(id+"F1.opExtrude","SWEPT_FACE",FACE,{"disambiguationData":[OSD([subQ0]),TDD([makeQuery(id+"F0.imprint","IMPRINT",EDGE,{"disambiguationData":[TD([[makeQuery(id+"F0.imprint","INTERSECT",VERTEX,{"derivedFrom":[subQ0,sQuery(id+"F0.wireOp",EDGE,"E10.2"),sQuery(id+"F0.wireOp",EDGE,"E18.1.1")]}),-1.0]])],"derivedFrom":subQ0})])]});}
            var Q13;
            {var subQ0=sQuery(id+"F0.wireOp",EDGE,"E18.1.1");Q13=makeQuery(id+"F4.boolean.opBoolean","MERGE",FACE,{"derivedFrom":[makeQuery(id+"F1.opExtrude","SWEPT_FACE",FACE,{"disambiguationData":[OSD([subQ0])]}),makeQuery(id+"F4.opExtrude","SWEPT_FACE",FACE,{"disambiguationData":[OSD([subQ0])]})]});}
            var Q14;
            {var subQ0=sQuery(id+"F0.wireOp",EDGE,"E15.0");Q14=makeQuery(id+"F4.opExtrude","SWEPT_FACE",FACE,{"disambiguationData":[OSD([subQ0]),TDD([makeQuery(id+"F0.imprint","IMPRINT",EDGE,{"disambiguationData":[TD([[makeQuery(id+"F0.imprint","INTERSECT",VERTEX,{"derivedFrom":[subQ0,sQuery(id+"F0.wireOp",EDGE,"E18.1.0")]}),1.0]])],"derivedFrom":subQ0})])]});}
            fillet(context, id + "F7", {"entities" : qUnion([Q0, Q1, Q2, Q3, Q4, Q5, Q6, Q7, Q8, Q9, Q10, Q11, Q12, Q13, Q14]), "radius" : 2 * mm, "tangentPropagation" : true, "allowEdgeOverflow" : false});
        }
    });
